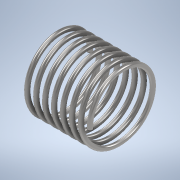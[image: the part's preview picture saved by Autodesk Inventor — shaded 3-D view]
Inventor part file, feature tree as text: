
AUTODESK INVENTOR PART (.ipt)
format: ipt  version: 2022 (Build 260153000, 153)  size: 355,840 bytes
history: native  units: in
note: dims shown in document units (in); Inventor stores cm internally (conversion verified against a paired STEP export)
features: sketch x3, helix x1, plane x1
ambient origin geometry x8: Origin, YZ Plane, XZ Plane, XY Plane, X Axis, Y Axis, Z Axis, Center Point
bodies: Solid1 (feature_tree)
feature tree (5):
  helix  "Coil1"  [1 undecoded]
  sketch  "Sketch2"  dims[d16=-0.0295in]
  plane  "Work Plane2"
  sketch  "Sketch5"  dims[d17=0.1575in]
  sketch  "Sketch1"  dims[d3=0.0197in d4=0.3937in d5=2.9528in d6=0.0in d7=90.0deg d8=90.0deg d9=0.0in d10=0.0in d11=0.1575in]
note: 1 required parameter value undecoded (feature->parameter linkage not recoverable at this tier; creation-order binding heuristic only, values carry confidence <= 0.55)
